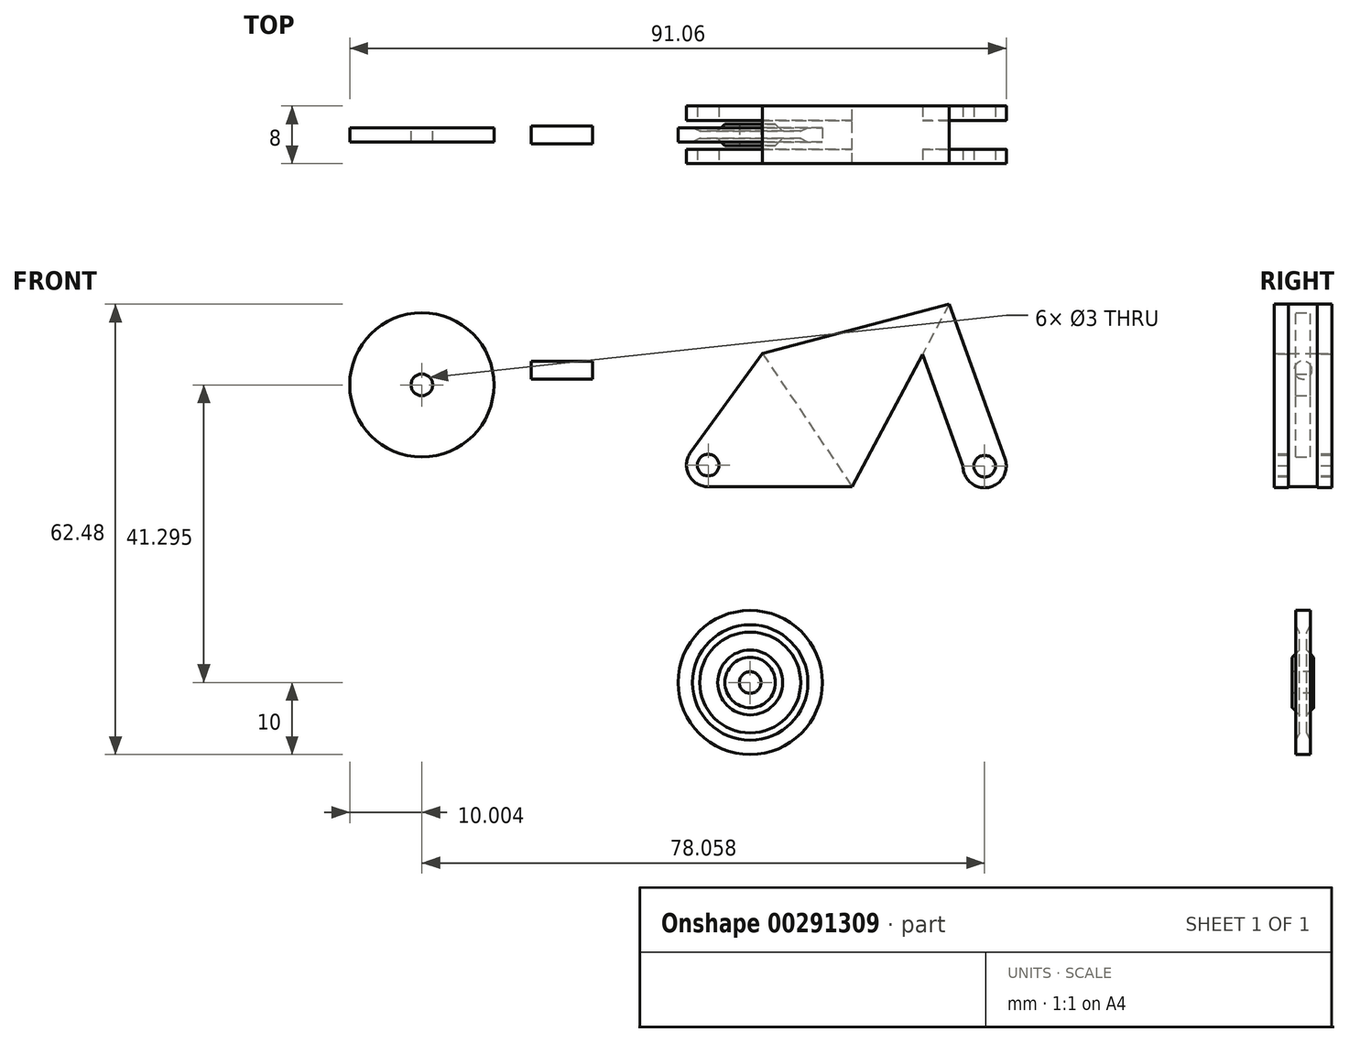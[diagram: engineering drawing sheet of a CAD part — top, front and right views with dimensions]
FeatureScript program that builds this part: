
annotation { "Feature Type Name" : "Feature", "Feature Type Description" : "" }
export const myFeature = defineFeature(function(context is Context, id is Id, definition is map)
    precondition{}
    {
        {
            var Q0;
            Q0=qCreatedBy(makeId("Front.planeOp"),FACE);
            var sketch = newSketch(context, id + "F0", { "sketchPlane" : qUnion([Q0])});
            skCircle(sketch, "E0", {"center": v(-45.54, 41.3) * mm, "radius": 10 * mm});
            skCircle(sketch, "E1", {"center": v(-45.54, 41.3) * mm, "radius": 1.5 * mm});
            skLineSegment(sketch, "E2.bottom", {"start": v(-30.37, 44.6) * mm, "end": v(-21.87, 44.6) * mm});
            skLineSegment(sketch, "E2.top", {"start": v(-30.37, 42.1) * mm, "end": v(-21.87, 42.1) * mm});
            skLineSegment(sketch, "E2.left", {"start": v(-30.37, 44.6) * mm, "end": v(-30.37, 42.1) * mm});
            skLineSegment(sketch, "E2.right", {"start": v(-21.87, 44.6) * mm, "end": v(-21.87, 42.1) * mm});
            skLineSegment(sketch, "E3", {"start": v(-21.87, 43.35) * mm, "end": v(-26.37, 43.35) * mm});
            skCircle(sketch, "E4", {"center": v(-26.37, 43.35) * mm, "radius": 5.5 * mm});
            skLineSegment(sketch, "E5", {"start": v(-21.87, 42.1) * mm, "end": v(-21.87, 41.1) * mm});
            skLineSegment(sketch, "E6.bottom", {"start": v(-21.87, 44.6) * mm, "end": v(-21.87, 44.6) * mm});
            skLineSegment(sketch, "E6.top", {"start": v(-21.87, 45.6) * mm, "end": v(-21.87, 45.6) * mm});
            skLineSegment(sketch, "E6.left", {"start": v(-21.87, 44.6) * mm, "end": v(-21.87, 45.6) * mm});
            skLineSegment(sketch, "E6.right", {"start": v(-21.87, 44.6) * mm, "end": v(-21.87, 45.6) * mm});
            skLineSegment(sketch, "E7", {"start": v(-21.87, 45.6) * mm, "end": v(-21.35, 45.6) * mm});
            skLineSegment(sketch, "E8", {"start": v(-21.87, 41.1) * mm, "end": v(-21.35, 41.1) * mm});
            skLineSegment(sketch, "E9", {"start": v(-26.37, 43.35) * mm, "end": v(-30.37, 43.35) * mm});
            skLineSegment(sketch, "E10", {"start": v(-21.87, 43.35) * mm, "end": v(-20.87, 43.35) * mm});
            skSolve(sketch);
        }
        {
            var Q0;
            Q0=makeQuery(id+"F0.imprint","IMPRINT",FACE,{"disambiguationData":[TD([[makeQuery(id+"F0.imprint","IMPRINT",EDGE,{"derivedFrom":sQuery(id+"F0.wireOp",EDGE,"E0")}),1.0]])]});
            extrude(context, id + "F1", {"entities" : qUnion([Q0]), "endBound" : BoundingType.SYMMETRIC, "depth" : 2 * mm});
        }
        {
            var Q0;
            {var subQ2=sQuery(id+"F0.wireOp",EDGE,"E2.bottom");Q0=makeQuery(id+"F0.imprint","IMPRINT",FACE,{"disambiguationData":[TD([[makeQuery(id+"F0.imprint","IMPRINT",EDGE,{"derivedFrom":subQ2}),-1.0]])]});}
            var Q1;
            {var subQ0=sQuery(id+"F0.wireOp",EDGE,"E6.right");Q1=makeQuery(id+"F0.imprint","IMPRINT",FACE,{"disambiguationData":[TD([[makeQuery(id+"F0.imprint","IMPRINT",EDGE,{"derivedFrom":subQ0}),-1.0]])]});}
            var Q2;
            Q2=sQuery(id+"F0.wireOp",EDGE,"E3");
            revolve(context, id + "F2", {"entities" : qUnion([Q0, Q1]), "axis" : qUnion([Q2]), "revolveType" : RevolveType.FULL});
        }
        {
            var Q0;
            Q0=qCreatedBy(makeId("Front.planeOp"),FACE);
            var sketch = newSketch(context, id + "F3", { "sketchPlane" : qUnion([Q0])});
            skLineSegment(sketch, "E11.bottom", {"start": v(1.67, 52.65) * mm, "end": v(35.17, 52.65) * mm});
            skLineSegment(sketch, "E11.top", {"start": v(1.67, 27.15) * mm, "end": v(35.17, 27.15) * mm});
            skLineSegment(sketch, "E11.left", {"start": v(1.67, 52.65) * mm, "end": v(1.67, 27.15) * mm});
            skLineSegment(sketch, "E11.right", {"start": v(35.17, 52.65) * mm, "end": v(35.17, 27.15) * mm});
            skLineSegment(sketch, "E12", {"start": v(35.17, 52.65) * mm, "end": v(27.67, 52.65) * mm});
            skLineSegment(sketch, "E13", {"start": v(1.67, 52.65) * mm, "end": v(1.67, 45.65) * mm});
            skLineSegment(sketch, "E14", {"start": v(1.67, 27.15) * mm, "end": v(14.17, 27.15) * mm});
            skLineSegment(sketch, "E15", {"start": v(1.67, 45.65) * mm, "end": v(14.17, 27.15) * mm});
            skLineSegment(sketch, "E16", {"start": v(14.17, 27.15) * mm, "end": v(27.67, 52.65) * mm});
            skLineSegment(sketch, "E17", {"start": v(27.69, 52.51) * mm, "end": v(1.67, 45.65) * mm});
            skSolve(sketch);
        }
        {
            var Q0;
            {var subQ0=sQuery(id+"F3.wireOp",EDGE,"E15");Q0=makeQuery(id+"F3.imprint","IMPRINT",FACE,{"disambiguationData":[TD([[makeQuery(id+"F3.imprint","IMPRINT",EDGE,{"derivedFrom":subQ0}),1.0]])]});}
            extrude(context, id + "F4", {"entities" : qUnion([Q0]), "endBound" : BoundingType.SYMMETRIC, "depth" : 8 * mm});
        }
        {
            var Q0;
            Q0=makeQuery(id+"F4.opExtrude","SWEPT_FACE",FACE,{"disambiguationData":[OSD([sQuery(id+"F3.wireOp",EDGE,"E15")])]});
            var sketch = newSketch(context, id + "F5", { "sketchPlane" : qUnion([Q0])});
            skLineSegment(sketch, "E18", {"start": v(-4, 36.9) * mm, "end": v(-2, 36.9) * mm});
            skLineSegment(sketch, "E19", {"start": v(4, 36.9) * mm, "end": v(2, 36.9) * mm});
            skLineSegment(sketch, "E20", {"start": v(-4, 14.56) * mm, "end": v(-2, 14.56) * mm});
            skLineSegment(sketch, "E21", {"start": v(4, 14.56) * mm, "end": v(2, 14.56) * mm});
            skLineSegment(sketch, "E22", {"start": v(-2, 36.9) * mm, "end": v(-2, 14.56) * mm});
            skLineSegment(sketch, "E23", {"start": v(2, 36.9) * mm, "end": v(2, 14.56) * mm});
            skSolve(sketch);
        }
        {
            var Q0;
            Q0=makeQuery(id+"F5.imprint","IMPRINT",FACE,{"disambiguationData":[TD([[makeQuery(id+"F5.imprint","IMPRINT",EDGE,{"derivedFrom":sQuery(id+"F5.wireOp",EDGE,"E19")}),1.0]])]});
            var Q1;
            Q1=makeQuery(id+"F5.imprint","IMPRINT",FACE,{"disambiguationData":[TD([[makeQuery(id+"F5.imprint","IMPRINT",EDGE,{"derivedFrom":sQuery(id+"F5.wireOp",EDGE,"E18")}),1.0]])]});
            extrude(context, id + "F6", {"entities" : qUnion([Q0, Q1]), "operationType" : NewBodyOperationType.ADD, "depth" : 25 * mm});
        }
        {
            var Q0;
            Q0=makeQuery(id+"F4.opExtrude","SWEPT_FACE",FACE,{"disambiguationData":[OSD([sQuery(id+"F3.wireOp",EDGE,"E16")])]});
            var sketch = newSketch(context, id + "F7", { "sketchPlane" : qUnion([Q0])});
            skLineSegment(sketch, "E24", {"start": v(-4, 59.29) * mm, "end": v(-2, 59.29) * mm});
            skLineSegment(sketch, "E25", {"start": v(-4, 30.63) * mm, "end": v(-2, 30.63) * mm});
            skLineSegment(sketch, "E26", {"start": v(2, 30.63) * mm, "end": v(4, 30.63) * mm});
            skLineSegment(sketch, "E27", {"start": v(2, 59.29) * mm, "end": v(4, 59.29) * mm});
            skLineSegment(sketch, "E28", {"start": v(2, 59.29) * mm, "end": v(2, 30.63) * mm});
            skLineSegment(sketch, "E29", {"start": v(-2, 30.63) * mm, "end": v(-2, 59.29) * mm});
            skSolve(sketch);
        }
        {
            var Q0;
            Q0 = qSketchRegion(id + "F7", true);
            var Q1;
            Q1=makeQuery(id+"F7.imprint","IMPRINT",FACE,{"disambiguationData":[TD([[makeQuery(id+"F7.imprint","IMPRINT",EDGE,{"derivedFrom":sQuery(id+"F7.wireOp",EDGE,"E26")}),1.0]])]});
            var Q2;
            Q2=makeQuery(id+"F7.imprint","IMPRINT",FACE,{"disambiguationData":[TD([[makeQuery(id+"F7.imprint","IMPRINT",EDGE,{"derivedFrom":sQuery(id+"F7.wireOp",EDGE,"E24")}),-1.0]])]});
            extrude(context, id + "F8", {"entities" : qUnion([Q0, Q1, Q2]), "operationType" : NewBodyOperationType.ADD, "depth" : 25 * mm});
        }
        {
            var Q0;
            {var subQ0=sQuery(id+"F3.wireOp",EDGE,"E16");var subQ1=sQuery(id+"F3.wireOp",EDGE,"E15");Q0=makeQuery(id+"F8.boolean.opBoolean","MERGE",FACE,{"derivedFrom":[makeQuery(id+"F6.boolean.opBoolean","MERGE",FACE,{"derivedFrom":[makeQuery(id+"F4.opExtrude","CAP_FACE",FACE,{"disambiguationData":[OSD([subQ1,subQ0,sQuery(id+"F3.wireOp",EDGE,"E17")])],"isStart":false}),makeQuery(id+"F6.opExtrude","SWEPT_FACE",FACE,{"disambiguationData":[OSD([subQ1]),TDD([makeQuery(id+"F5.imprint","IMPRINT",EDGE,{"derivedFrom":makeQuery(id+"F4.opExtrude","CAP_EDGE",EDGE,{"disambiguationData":[OSD([subQ1])],"isStart":false})})])]})]}),makeQuery(id+"F8.opExtrude","SWEPT_FACE",FACE,{"disambiguationData":[OSD([subQ0]),TDD([makeQuery(id+"F7.imprint","IMPRINT",EDGE,{"derivedFrom":makeQuery(id+"F4.opExtrude","CAP_EDGE",EDGE,{"disambiguationData":[OSD([subQ0])],"isStart":false})})])]})]});}
            var sketch = newSketch(context, id + "F9", { "sketchPlane" : qUnion([Q0])});
            skLineSegment(sketch, "E30", {"start": v(14.17, 27.15) * mm, "end": v(-5.83, 27.15) * mm});
            skLineSegment(sketch, "E31", {"start": v(-5.83, 27.15) * mm, "end": v(-5.83, 30.15) * mm});
            skCircle(sketch, "E32", {"center": v(-5.83, 30.15) * mm, "radius": 3 * mm});
            skLineSegment(sketch, "E33", {"start": v(1.67, 45.65) * mm, "end": v(-8.26, 31.9) * mm});
            skCircle(sketch, "E34", {"center": v(-5.83, 30.15) * mm, "radius": 1.5 * mm});
            skLineSegment(sketch, "E35", {"start": v(27.58, 52.48) * mm, "end": v(25.73, 48.98) * mm});
            skLineSegment(sketch, "E36", {"start": v(27.58, 52.48) * mm, "end": v(14.17, 27.15) * mm});
            skLineSegment(sketch, "E37", {"start": v(25.73, 48.98) * mm, "end": v(25.73, 28.8) * mm});
            skLineSegment(sketch, "E38", {"start": v(25.73, 48.98) * mm, "end": v(32.52, 30.01) * mm});
            skCircle(sketch, "E39", {"center": v(32.52, 30.01) * mm, "radius": 3 * mm});
            skCircle(sketch, "E40", {"center": v(32.52, 30.01) * mm, "radius": 1.5 * mm});
            skLineSegment(sketch, "E41", {"start": v(27.58, 52.48) * mm, "end": v(35.34, 31.03) * mm});
            skLineSegment(sketch, "E42", {"start": v(32.52, 30.01) * mm, "end": v(29.52, 30.01) * mm});
            skLineSegment(sketch, "E43", {"start": v(29.52, 30.01) * mm, "end": v(23.9, 45.54) * mm});
            skSolve(sketch);
        }
        {
            var Q0;
            {var subQ2=sQuery(id+"F9.wireOp",EDGE,"E30");Q0=makeQuery(id+"F9.imprint","IMPRINT",FACE,{"disambiguationData":[TD([[makeQuery(id+"F9.imprint","IMPRINT",EDGE,{"derivedFrom":subQ2}),1.0]])]});}
            var Q1;
            {var subQ4=sQuery(id+"F9.wireOp",EDGE,"E41");Q1=makeQuery(id+"F9.imprint","IMPRINT",FACE,{"disambiguationData":[TD([[makeQuery(id+"F9.imprint","IMPRINT",EDGE,{"derivedFrom":subQ4}),1.0]])]});}
            var Q2;
            Q2=makeQuery(id+"F9.imprint","IMPRINT",FACE,{"disambiguationData":[TD([[makeQuery(id+"F9.imprint","IMPRINT",EDGE,{"derivedFrom":sQuery(id+"F9.wireOp",EDGE,"E34")}),1.0]])]});
            var Q3;
            {var subQ0=sQuery(id+"F9.wireOp",EDGE,"E42");var subQ1=sQuery(id+"F9.wireOp",EDGE,"E38");var subQ2=makeQuery(id+"F9.imprint","INTERSECT",VERTEX,{"derivedFrom":[subQ1,subQ0]});Q3=makeQuery(id+"F9.imprint","IMPRINT",FACE,{"disambiguationData":[TD([[makeQuery(id+"F9.imprint","IMPRINT",EDGE,{"disambiguationData":[TD([[subQ2,1.0]])],"derivedFrom":subQ1}),1.0]])]});}
            var Q4;
            {var subQ0=sQuery(id+"F9.wireOp",EDGE,"E42");var subQ1=sQuery(id+"F9.wireOp",EDGE,"E38");var subQ2=makeQuery(id+"F9.imprint","INTERSECT",VERTEX,{"derivedFrom":[subQ1,subQ0]});Q4=makeQuery(id+"F9.imprint","IMPRINT",FACE,{"disambiguationData":[TD([[makeQuery(id+"F9.imprint","IMPRINT",EDGE,{"disambiguationData":[TD([[subQ2,1.0]])],"derivedFrom":subQ1}),-1.0]])]});}
            extrude(context, id + "F10", {"entities" : qUnion([Q0, Q1, Q2, Q3, Q4]), "operationType" : NewBodyOperationType.REMOVE, "oppositeDirection" : true, "depth" : 8 * mm});
        }
        {
            var Q0;
            Q0=qCreatedBy(makeId("Right.planeOp"),FACE);
            var sketch = newSketch(context, id + "F11", { "sketchPlane" : qUnion([Q0])});
            skLineSegment(sketch, "E44", {"start": v(0, 0) * mm, "end": v(1, 0) * mm});
            skLineSegment(sketch, "E45", {"start": v(0, 0) * mm, "end": v(-1, 0) * mm});
            skLineSegment(sketch, "E46", {"start": v(1, 0) * mm, "end": v(1, 10) * mm});
            skLineSegment(sketch, "E47", {"start": v(1, 10) * mm, "end": v(-1, 10) * mm});
            skLineSegment(sketch, "E48", {"start": v(-1, 10) * mm, "end": v(-1, 0) * mm});
            skLineSegment(sketch, "E49", {"start": v(1, 10) * mm, "end": v(1, 8) * mm});
            skLineSegment(sketch, "E50", {"start": v(-1, 10) * mm, "end": v(-1, 8) * mm});
            skLineSegment(sketch, "E51", {"start": v(0, 0) * mm, "end": v(0, 1.5) * mm});
            skLineSegment(sketch, "E52", {"start": v(0, 1.5) * mm, "end": v(1, 1.5) * mm});
            skLineSegment(sketch, "E53", {"start": v(0, 1.5) * mm, "end": v(-1, 1.5) * mm});
            skLineSegment(sketch, "E54", {"start": v(1, 1.5) * mm, "end": v(1.5, 1.5) * mm});
            skLineSegment(sketch, "E55", {"start": v(-1, 1.5) * mm, "end": v(-1.5, 1.5) * mm});
            skLineSegment(sketch, "E56", {"start": v(1.5, 1.5) * mm, "end": v(1.5, 3.5) * mm});
            skLineSegment(sketch, "E57", {"start": v(-1.5, 1.5) * mm, "end": v(-1.5, 3.5) * mm});
            skLineSegment(sketch, "E58", {"start": v(1, 8) * mm, "end": v(0.5, 8) * mm});
            skLineSegment(sketch, "E59", {"start": v(-1, 8) * mm, "end": v(-0.5, 8) * mm});
            skLineSegment(sketch, "E60", {"start": v(-0.5, 8) * mm, "end": v(-0.5, 7) * mm});
            skLineSegment(sketch, "E61", {"start": v(0.5, 8) * mm, "end": v(0.5, 7) * mm});
            skLineSegment(sketch, "E62", {"start": v(1.5, 3.5) * mm, "end": v(0.5, 3.5) * mm});
            skLineSegment(sketch, "E63", {"start": v(-1.5, 3.5) * mm, "end": v(-0.5, 3.5) * mm});
            skLineSegment(sketch, "E64", {"start": v(0.5, 3.5) * mm, "end": v(0.5, 4.5) * mm});
            skLineSegment(sketch, "E65", {"start": v(-0.5, 3.5) * mm, "end": v(-0.5, 4.5) * mm});
            skLineSegment(sketch, "E66", {"start": v(1.5, 3.5) * mm, "end": v(0.5, 4.5) * mm});
            skLineSegment(sketch, "E67", {"start": v(-0.5, 4.5) * mm, "end": v(-1.5, 3.5) * mm});
            skLineSegment(sketch, "E68", {"start": v(-0.5, 4.5) * mm, "end": v(-0.5, 7) * mm});
            skLineSegment(sketch, "E69", {"start": v(1, 8) * mm, "end": v(0.5, 7) * mm});
            skLineSegment(sketch, "E70", {"start": v(0.5, 7) * mm, "end": v(0.5, 4.5) * mm});
            skLineSegment(sketch, "E71", {"start": v(-1, 8) * mm, "end": v(-0.5, 7) * mm});
            skSolve(sketch);
        }
        {
            var Q0;
            Q0=makeQuery(id+"F11.imprint","IMPRINT",FACE,{"disambiguationData":[TD([[makeQuery(id+"F11.imprint","IMPRINT",EDGE,{"derivedFrom":sQuery(id+"F11.wireOp",EDGE,"E47")}),1.0]])]});
            var Q1;
            {var subQ0=sQuery(id+"F11.wireOp",EDGE,"E54");Q1=makeQuery(id+"F11.imprint","IMPRINT",FACE,{"disambiguationData":[TD([[makeQuery(id+"F11.imprint","IMPRINT",EDGE,{"derivedFrom":subQ0}),1.0]])]});}
            var Q2;
            {var subQ0=sQuery(id+"F11.wireOp",EDGE,"E66");var subQ1=sQuery(id+"F11.wireOp",EDGE,"E46");var subQ2=makeQuery(id+"F11.imprint","INTERSECT",VERTEX,{"derivedFrom":[subQ1,subQ0]});Q2=makeQuery(id+"F11.imprint","IMPRINT",FACE,{"disambiguationData":[TD([[makeQuery(id+"F11.imprint","IMPRINT",EDGE,{"disambiguationData":[TD([[subQ2,1.0]])],"derivedFrom":subQ1}),-1.0]])]});}
            var Q3;
            {var subQ5=sQuery(id+"F11.wireOp",EDGE,"E64");Q3=makeQuery(id+"F11.imprint","IMPRINT",FACE,{"disambiguationData":[TD([[makeQuery(id+"F11.imprint","IMPRINT",EDGE,{"derivedFrom":subQ5}),-1.0]])]});}
            var Q4;
            {var subQ5=sQuery(id+"F11.wireOp",EDGE,"E65");Q4=makeQuery(id+"F11.imprint","IMPRINT",FACE,{"disambiguationData":[TD([[makeQuery(id+"F11.imprint","IMPRINT",EDGE,{"derivedFrom":subQ5}),1.0]])]});}
            var Q5;
            {var subQ0=sQuery(id+"F11.wireOp",EDGE,"E67");var subQ1=sQuery(id+"F11.wireOp",EDGE,"E48");var subQ2=makeQuery(id+"F11.imprint","INTERSECT",VERTEX,{"derivedFrom":[subQ1,subQ0]});Q5=makeQuery(id+"F11.imprint","IMPRINT",FACE,{"disambiguationData":[TD([[makeQuery(id+"F11.imprint","IMPRINT",EDGE,{"disambiguationData":[TD([[subQ2,-1.0]])],"derivedFrom":subQ1}),-1.0]])]});}
            var Q6;
            {var subQ0=sQuery(id+"F11.wireOp",EDGE,"E55");Q6=makeQuery(id+"F11.imprint","IMPRINT",FACE,{"disambiguationData":[TD([[makeQuery(id+"F11.imprint","IMPRINT",EDGE,{"derivedFrom":subQ0}),-1.0]])]});}
            var Q7;
            Q7=makeQuery(id+"F11.imprint","IMPRINT",FACE,{"disambiguationData":[TD([[makeQuery(id+"F11.imprint","IMPRINT",EDGE,{"derivedFrom":sQuery(id+"F11.wireOp",EDGE,"E58")}),1.0]])]});
            var Q8;
            Q8=makeQuery(id+"F11.imprint","IMPRINT",FACE,{"disambiguationData":[TD([[makeQuery(id+"F11.imprint","IMPRINT",EDGE,{"derivedFrom":sQuery(id+"F11.wireOp",EDGE,"E59")}),-1.0]])]});
            var Q9;
            Q9=sQuery(id+"F11.wireOp",EDGE,"E44");
            revolve(context, id + "F12", {"entities" : qUnion([Q0, Q1, Q2, Q3, Q4, Q5, Q6, Q7, Q8]), "axis" : qUnion([Q9]), "revolveType" : RevolveType.FULL});
        }
    });
